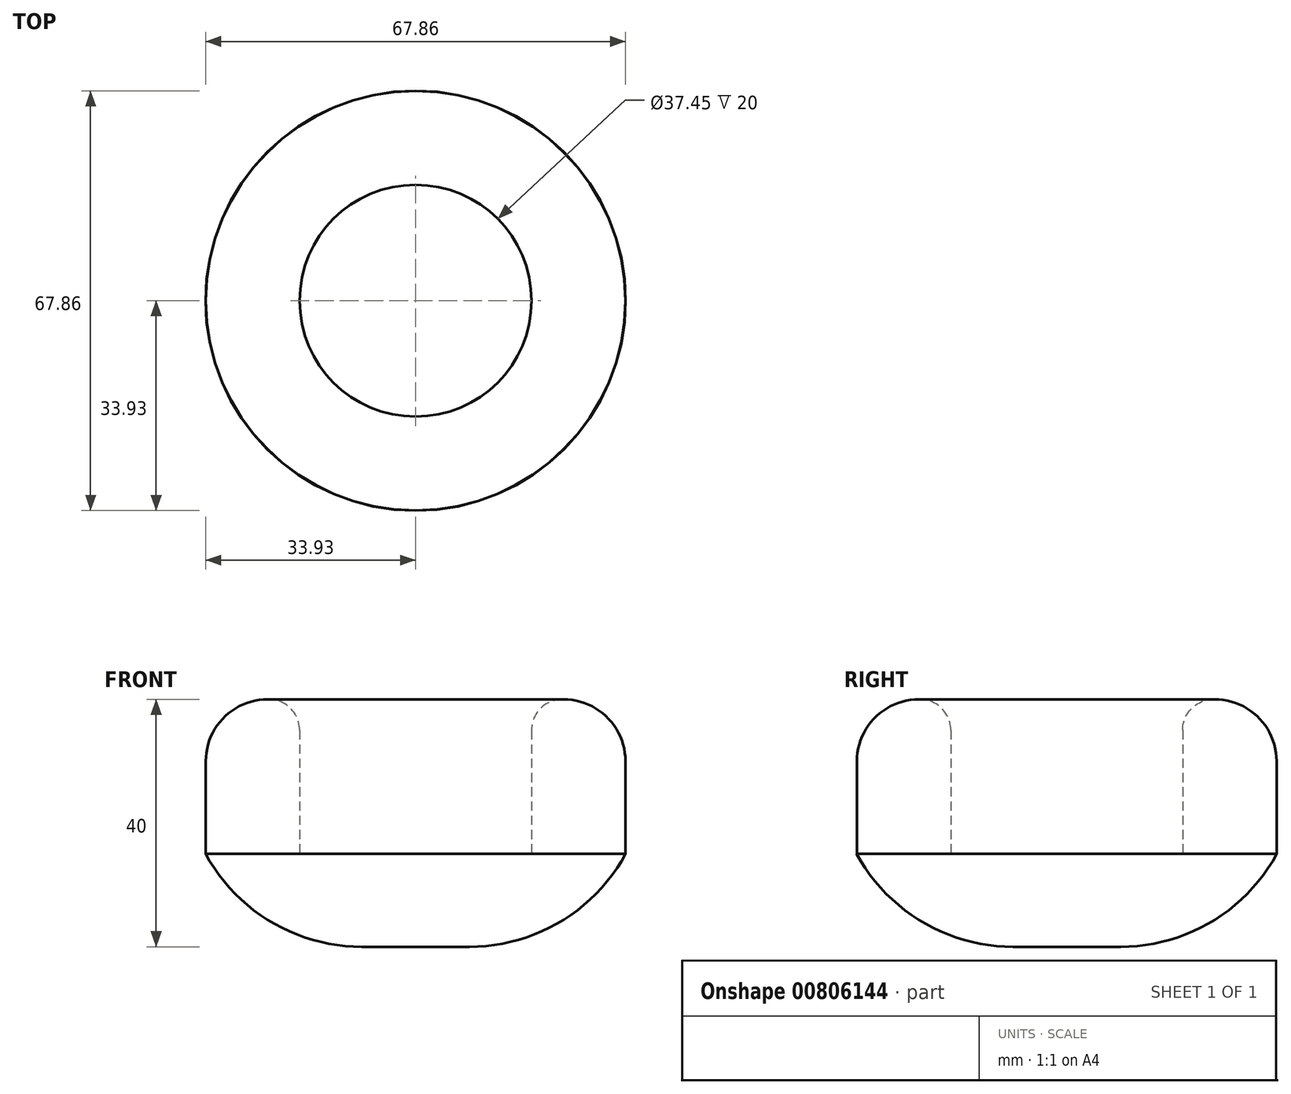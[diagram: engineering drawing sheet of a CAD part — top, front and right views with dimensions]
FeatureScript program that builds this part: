
annotation { "Feature Type Name" : "Feature", "Feature Type Description" : "" }
export const myFeature = defineFeature(function(context is Context, id is Id, definition is map)
    precondition{}
    {
        {
            var Q0;
            Q0=qCreatedBy(makeId("Top.planeOp"),FACE);
            var sketch = newSketch(context, id + "F0", { "sketchPlane" : qUnion([Q0])});
            skCircle(sketch, "E0", {"center": v(0, 0) * mm, "radius": 18.73 * mm});
            skCircle(sketch, "E1", {"center": v(0, 0) * mm, "radius": 33.9 * mm});
            skSolve(sketch);
        }
        {
            var Q0;
            Q0=makeQuery(id+"F0.imprint","IMPRINT",FACE,{"disambiguationData":[TD([[makeQuery(id+"F0.imprint","IMPRINT",EDGE,{"derivedFrom":sQuery(id+"F0.wireOp",EDGE,"E0")}),-1.0]])]});
            extrude(context, id + "F1", {"entities" : qUnion([Q0]), "depth" : 40 * mm, "offsetDistance" : 25 * mm});
        }
        {
            var Q0;
            Q0=qCreatedBy(makeId("Top.planeOp"),FACE);
            var sketch = newSketch(context, id + "F2", { "sketchPlane" : qUnion([Q0])});
            skCircle(sketch, "E2", {"center": v(0, 0) * mm, "radius": 33.93 * mm});
            skSolve(sketch);
        }
        {
            var Q0;
            Q0=makeQuery(id+"F2.imprint","IMPRINT",FACE,{"disambiguationData":[TD([[makeQuery(id+"F2.imprint","IMPRINT",EDGE,{"derivedFrom":sQuery(id+"F2.wireOp",EDGE,"E2")}),1.0]])]});
            extrude(context, id + "F3", {"entities" : qUnion([Q0]), "operationType" : NewBodyOperationType.ADD, "depth" : 15 * mm, "offsetDistance" : 25 * mm});
        }
        {
            var Q0;
            Q0=makeQuery(id+"F1.opExtrude","CAP_EDGE",EDGE,{"disambiguationData":[OSD([sQuery(id+"F0.wireOp",EDGE,"E1")])],"isStart":false});
            fillet(context, id + "F4", {"entities" : qUnion([Q0]), "radius" : 10 * mm, "tangentPropagation" : true, "allowEdgeOverflow" : false});
        }
        {
            var Q0;
            Q0=makeQuery(id+"F1.opExtrude","CAP_EDGE",EDGE,{"disambiguationData":[OSD([sQuery(id+"F0.wireOp",EDGE,"E0")])],"isStart":false});
            fillet(context, id + "F5", {"entities" : qUnion([Q0]), "radius" : 5 * mm, "tangentPropagation" : true, "allowEdgeOverflow" : false});
        }
        {
            var Q0;
            Q0=makeQuery(id+"F3.opExtrude","CAP_EDGE",EDGE,{"disambiguationData":[OSD([sQuery(id+"F2.wireOp",EDGE,"E2")])],"isStart":true});
            fillet(context, id + "F6", {"entities" : qUnion([Q0]), "radius" : 28.73 * mm, "tangentPropagation" : true, "allowEdgeOverflow" : false});
        }
    });
